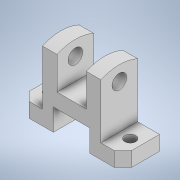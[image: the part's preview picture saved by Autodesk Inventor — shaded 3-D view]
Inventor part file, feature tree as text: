
AUTODESK INVENTOR PART (.ipt)
format: ipt  version: 2022.2 (Build 262287030, 287C)  size: 171,520 bytes
history: native  units: in
note: dims shown in document units (in); Inventor stores cm internally (conversion verified against a paired STEP export)
features: extrude x4, sketch x4
ambient origin geometry x8: Origin, YZ Plane, XZ Plane, XY Plane, X Axis, Y Axis, Z Axis, Center Point
bodies: Solid1 (feature_tree)
feature tree (8):
  extrude  "Extrusion1"  Depth=1.25in
  extrude  "Extrusion2"  Depth=0.5in
  extrude  "Extrusion3"  Depth=0.75in
  extrude  "Extrusion4"  Depth=1.25in
  sketch  "Sketch2"  dims[d2=1.5in d4=1.25in]
  sketch  "Sketch3"  dims[d5=2.0in d6=0.5in]
  sketch  "Sketch4"  dims[d7=3.5in d8=0.0in d9=0.75in]
  sketch  "Sketch5"  dims[d10=1.0in d11=1.25in d12=0.75in d13=0.5in d14=2.0in d15=0.0in d16=0.0in d17=1.5in d18=0.5in d19=0.0in d20=0.0in d21=0.375in d22=0.375in d24=0.625in d25=0.3in d26=0.3in d27=0.0in d28=0.0in]
